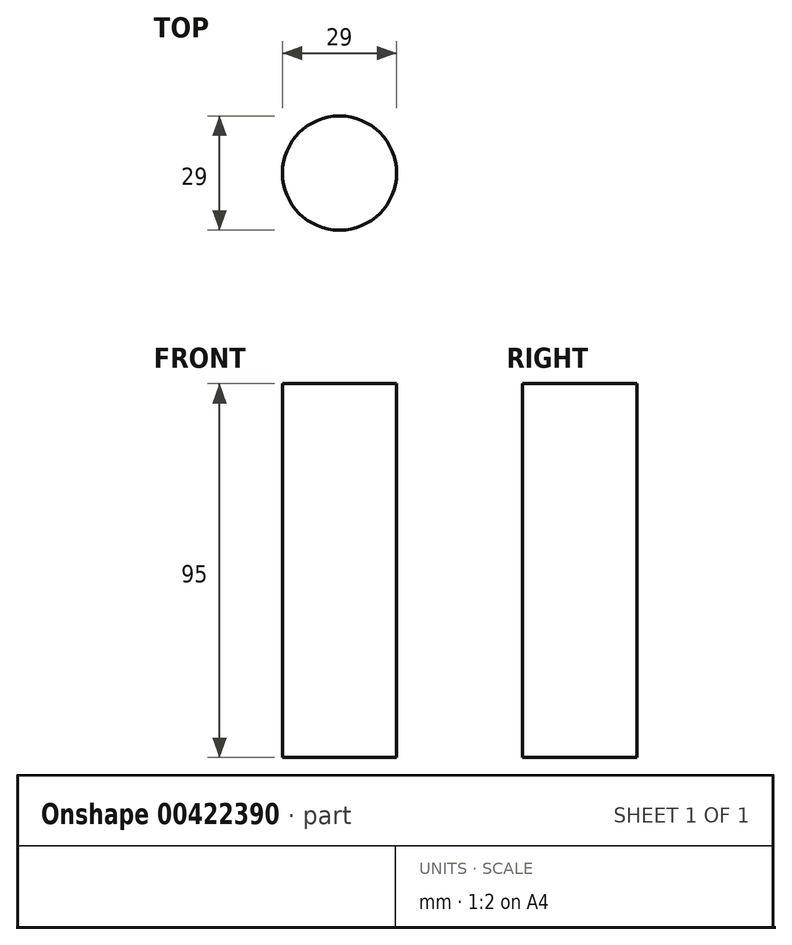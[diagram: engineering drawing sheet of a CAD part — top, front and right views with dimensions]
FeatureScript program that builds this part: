
annotation { "Feature Type Name" : "Feature", "Feature Type Description" : "" }
export const myFeature = defineFeature(function(context is Context, id is Id, definition is map)
    precondition{}
    {
        {
            var Q0;
            Q0=qCreatedBy(makeId("Top.planeOp"),FACE);
            var sketch = newSketch(context, id + "F0", { "sketchPlane" : qUnion([Q0])});
            skCircle(sketch, "E0", {"center": v(0, 0) * mm, "radius": 14.5 * mm});
            skSolve(sketch);
        }
        {
            var Q0;
            Q0=makeQuery(id+"F0.imprint","IMPRINT",FACE,{"disambiguationData":[TD([[makeQuery(id+"F0.imprint","IMPRINT",EDGE,{"derivedFrom":sQuery(id+"F0.wireOp",EDGE,"E0")}),1.0]])]});
            extrude(context, id + "F1", {"entities" : qUnion([Q0]), "endBound" : BoundingType.SYMMETRIC, "depth" : 95 * mm});
        }
    });
